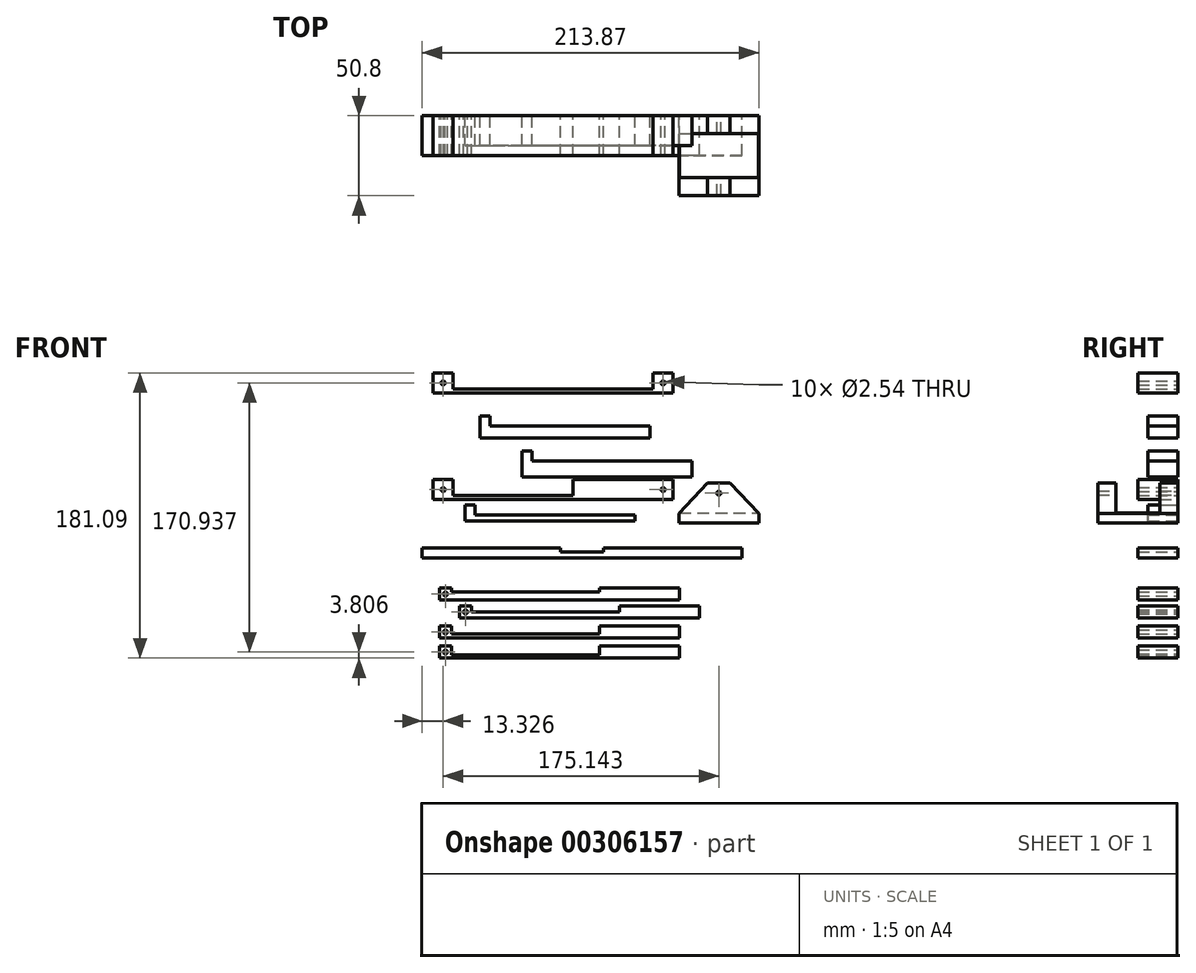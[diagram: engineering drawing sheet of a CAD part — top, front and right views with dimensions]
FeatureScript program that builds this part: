
annotation { "Feature Type Name" : "Feature", "Feature Type Description" : "" }
export const myFeature = defineFeature(function(context is Context, id is Id, definition is map)
    precondition{}
    {
        {
            var Q0;
            Q0=qCreatedBy(makeId("Front.planeOp"),FACE);
            var sketch = newSketch(context, id + "F0", { "sketchPlane" : qUnion([Q0])});
            skLineSegment(sketch, "E0", {"start": v(-69.54, -19.01) * mm, "end": v(133.66, -19.01) * mm});
            skLineSegment(sketch, "E1", {"start": v(133.66, -19.01) * mm, "end": v(133.66, -12.66) * mm});
            skLineSegment(sketch, "E2", {"start": v(133.66, -12.66) * mm, "end": v(45.7, -12.66) * mm});
            skLineSegment(sketch, "E3", {"start": v(45.7, -12.66) * mm, "end": v(45.7, -15.2) * mm});
            skLineSegment(sketch, "E4", {"start": v(45.7, -15.2) * mm, "end": v(18.4, -15.2) * mm});
            skLineSegment(sketch, "E5", {"start": v(18.4, -15.2) * mm, "end": v(18.4, -12.66) * mm});
            skLineSegment(sketch, "E6", {"start": v(18.4, -12.66) * mm, "end": v(-69.54, -12.66) * mm});
            skLineSegment(sketch, "E7", {"start": v(-69.54, -12.66) * mm, "end": v(-69.54, -19.01) * mm});
            skSolve(sketch);
        }
        {
            var Q0;
            Q0 = qSketchRegion(id + "F0", true);
            extrude(context, id + "F1", {"entities" : qUnion([Q0]), "depth" : 25.4 * mm});
        }
        {
            var Q0;
            Q0=qCreatedBy(makeId("Front.planeOp"),FACE);
            var sketch = newSketch(context, id + "F2", { "sketchPlane" : qUnion([Q0])});
            skLineSegment(sketch, "E8", {"start": v(-62.56, 18.1) * mm, "end": v(89.84, 18.1) * mm});
            skLineSegment(sketch, "E9", {"start": v(89.84, 18.1) * mm, "end": v(89.84, 30.8) * mm});
            skLineSegment(sketch, "E10", {"start": v(89.84, 30.8) * mm, "end": v(77.14, 30.8) * mm});
            skLineSegment(sketch, "E11", {"start": v(77.14, 30.8) * mm, "end": v(77.14, 20.64) * mm});
            skLineSegment(sketch, "E12", {"start": v(77.14, 20.64) * mm, "end": v(-49.86, 20.64) * mm});
            skLineSegment(sketch, "E13", {"start": v(-49.86, 20.64) * mm, "end": v(-49.86, 30.8) * mm});
            skLineSegment(sketch, "E14", {"start": v(-49.86, 30.8) * mm, "end": v(-62.56, 30.8) * mm});
            skLineSegment(sketch, "E15", {"start": v(-62.56, 30.8) * mm, "end": v(-62.56, 18.1) * mm});
            skCircle(sketch, "E16", {"center": v(-56.21, 24.45) * mm, "radius": 1.27 * mm});
            skPoint(sketch, "E16.centerSnap0", {"position": v(-56.21, 30.8) * mm});
            skPoint(sketch, "E16.centerSnap1", {"position": v(-62.56, 24.45) * mm});
            skCircle(sketch, "E17", {"center": v(83.49, 24.45) * mm, "radius": 1.27 * mm});
            skPoint(sketch, "E17.centerSnap0", {"position": v(89.84, 24.45) * mm});
            skPoint(sketch, "E17.centerSnap1", {"position": v(83.49, 30.8) * mm});
            skSolve(sketch);
        }
        {
            var Q0;
            Q0 = qSketchRegion(id + "F2", true);
            extrude(context, id + "F3", {"entities" : qUnion([Q0]), "depth" : 25.4 * mm});
        }
        {
            var Q0;
            Q0=qCreatedBy(makeId("Front.planeOp"),FACE);
            var sketch = newSketch(context, id + "F4", { "sketchPlane" : qUnion([Q0])});
            skLineSegment(sketch, "E18", {"start": v(111.75, 28.6) * mm, "end": v(126.1, 28.6) * mm});
            skLineSegment(sketch, "E19", {"start": v(126.1, 28.6) * mm, "end": v(144.33, 9.27) * mm});
            skLineSegment(sketch, "E20", {"start": v(144.33, 9.27) * mm, "end": v(144.33, 3.2) * mm});
            skLineSegment(sketch, "E21", {"start": v(144.33, 3.2) * mm, "end": v(93.53, 3.2) * mm});
            skLineSegment(sketch, "E22", {"start": v(93.53, 3.2) * mm, "end": v(93.53, 9.27) * mm});
            skLineSegment(sketch, "E23", {"start": v(93.53, 9.27) * mm, "end": v(111.75, 28.6) * mm});
            skCircle(sketch, "E24", {"center": v(118.93, 22.25) * mm, "radius": 1.27 * mm});
            skSolve(sketch);
        }
        {
            var Q0;
            Q0 = qSketchRegion(id + "F4", true);
            extrude(context, id + "F5", {"entities" : qUnion([Q0]), "depth" : 50.8 * mm});
        }
        {
            var Q0;
            Q0=makeQuery(id+"F5.opExtrude","SWEPT_FACE",FACE,{"disambiguationData":[OSD([sQuery(id+"F4.wireOp",EDGE,"E18")])]});
            var sketch = newSketch(context, id + "F6", { "sketchPlane" : qUnion([Q0])});
            skLineSegment(sketch, "E25.bottom", {"start": v(93.53, -11.43) * mm, "end": v(144.33, -11.43) * mm});
            skLineSegment(sketch, "E25.top", {"start": v(93.53, -39.37) * mm, "end": v(144.33, -39.37) * mm});
            skLineSegment(sketch, "E25.left", {"start": v(93.53, -11.43) * mm, "end": v(93.53, -39.37) * mm});
            skLineSegment(sketch, "E25.right", {"start": v(144.33, -11.43) * mm, "end": v(144.33, -39.37) * mm});
            skSolve(sketch);
        }
        {
            var Q0;
            Q0 = qSketchRegion(id + "F6", true);
            extrude(context, id + "F7", {"entities" : qUnion([Q0]), "operationType" : NewBodyOperationType.REMOVE, "oppositeDirection" : true, "depth" : 19.05 * mm});
        }
        {
            var Q0;
            Q0=makeQuery(id+"F5.opExtrude","SWEPT_BODY",BODY,{"disambiguationData":[OSD([sQuery(id+"F4.wireOp",EDGE,"E18"),sQuery(id+"F4.wireOp",EDGE,"E19"),sQuery(id+"F4.wireOp",EDGE,"E20"),sQuery(id+"F4.wireOp",EDGE,"E21"),sQuery(id+"F4.wireOp",EDGE,"E22"),sQuery(id+"F4.wireOp",EDGE,"E23"),sQuery(id+"F4.wireOp",EDGE,"E24")])]});
            transform(context, id + "F8", {"entities" : qUnion([Q0]), "transformType" : TransformType.TRANSLATION_3D, "dx" : 60.96 * mm, "dy" : 0 * mm, "dz" : 0 * mm, "makeCopy" : true});
        }
        {
            var Q0;
            Q0=makeQuery(id+"F3.opExtrude","SWEPT_BODY",BODY,{"disambiguationData":[OSD([sQuery(id+"F2.wireOp",EDGE,"E8"),sQuery(id+"F2.wireOp",EDGE,"E9"),sQuery(id+"F2.wireOp",EDGE,"E10"),sQuery(id+"F2.wireOp",EDGE,"E11"),sQuery(id+"F2.wireOp",EDGE,"E12"),sQuery(id+"F2.wireOp",EDGE,"E13"),sQuery(id+"F2.wireOp",EDGE,"E14"),sQuery(id+"F2.wireOp",EDGE,"E15"),sQuery(id+"F2.wireOp",EDGE,"E16"),sQuery(id+"F2.wireOp",EDGE,"E17")])]});
            transform(context, id + "F9", {"entities" : qUnion([Q0]), "transformType" : TransformType.TRANSLATION_3D, "dx" : 0 * mm, "dy" : 0 * mm, "dz" : 67.82 * mm, "makeCopy" : true});
        }
        {
            var Q0;
            Q0=makeQuery(id+"F3.opExtrude","SWEPT_BODY",BODY,{"disambiguationData":[OSD([sQuery(id+"F2.wireOp",EDGE,"E8"),sQuery(id+"F2.wireOp",EDGE,"E9"),sQuery(id+"F2.wireOp",EDGE,"E10"),sQuery(id+"F2.wireOp",EDGE,"E11"),sQuery(id+"F2.wireOp",EDGE,"E12"),sQuery(id+"F2.wireOp",EDGE,"E13"),sQuery(id+"F2.wireOp",EDGE,"E14"),sQuery(id+"F2.wireOp",EDGE,"E15"),sQuery(id+"F2.wireOp",EDGE,"E16"),sQuery(id+"F2.wireOp",EDGE,"E17")])]});
            transform(context, id + "F10", {"entities" : qUnion([Q0]), "transformType" : TransformType.TRANSLATION_3D, "dx" : 0 * mm, "dy" : 0 * mm, "dz" : 33.78 * mm, "makeCopy" : true});
        }
        {
            var Q0;
            Q0=makeQuery(id+"F10.opPattern","COPY",BODY,{"derivedFrom":makeQuery(id+"F3.opExtrude","SWEPT_BODY",BODY,{"disambiguationData":[OSD([sQuery(id+"F2.wireOp",EDGE,"E8"),sQuery(id+"F2.wireOp",EDGE,"E9"),sQuery(id+"F2.wireOp",EDGE,"E10"),sQuery(id+"F2.wireOp",EDGE,"E11"),sQuery(id+"F2.wireOp",EDGE,"E12"),sQuery(id+"F2.wireOp",EDGE,"E13"),sQuery(id+"F2.wireOp",EDGE,"E14"),sQuery(id+"F2.wireOp",EDGE,"E15"),sQuery(id+"F2.wireOp",EDGE,"E16"),sQuery(id+"F2.wireOp",EDGE,"E17")])]}),"instanceName":"1"});
            deleteBodies(context, id + "F11", {"entities" : qUnion([Q0])});
        }
        {
            var Q0;
            Q0=makeQuery(id+"F8.opPattern","COPY",BODY,{"derivedFrom":makeQuery(id+"F5.opExtrude","SWEPT_BODY",BODY,{"disambiguationData":[OSD([sQuery(id+"F4.wireOp",EDGE,"E18"),sQuery(id+"F4.wireOp",EDGE,"E19"),sQuery(id+"F4.wireOp",EDGE,"E20"),sQuery(id+"F4.wireOp",EDGE,"E21"),sQuery(id+"F4.wireOp",EDGE,"E22"),sQuery(id+"F4.wireOp",EDGE,"E23"),sQuery(id+"F4.wireOp",EDGE,"E24")])]}),"instanceName":"1"});
            deleteBodies(context, id + "F12", {"entities" : qUnion([Q0])});
        }
        {
            var Q0;
            Q0=makeQuery(id+"F3.opExtrude","SWEPT_FACE",FACE,{"disambiguationData":[OSD([sQuery(id+"F2.wireOp",EDGE,"E11")])]});
            extrude(context, id + "F13", {"entities" : qUnion([Q0]), "operationType" : NewBodyOperationType.ADD, "depth" : 50.8 * mm});
        }
        {
            var Q0;
            Q0=qCreatedBy(makeId("Front.planeOp"),FACE);
            var sketch = newSketch(context, id + "F14", { "sketchPlane" : qUnion([Q0])});
            skLineSegment(sketch, "E26", {"start": v(-45.79, -49.45) * mm, "end": v(-45.79, -57.07) * mm});
            skLineSegment(sketch, "E27", {"start": v(-45.79, -57.07) * mm, "end": v(106.61, -57.07) * mm});
            skLineSegment(sketch, "E28", {"start": v(106.61, -57.07) * mm, "end": v(106.61, -49.45) * mm});
            skLineSegment(sketch, "E29", {"start": v(106.61, -49.45) * mm, "end": v(55.81, -49.45) * mm});
            skLineSegment(sketch, "E30", {"start": v(55.81, -49.45) * mm, "end": v(55.81, -53.26) * mm});
            skLineSegment(sketch, "E31", {"start": v(55.81, -53.26) * mm, "end": v(-38.17, -53.26) * mm});
            skLineSegment(sketch, "E32", {"start": v(-38.17, -53.26) * mm, "end": v(-38.17, -49.45) * mm});
            skLineSegment(sketch, "E33", {"start": v(-38.17, -49.45) * mm, "end": v(-45.79, -49.45) * mm});
            skCircle(sketch, "E34", {"center": v(-41.98, -53.26) * mm, "radius": 1.27 * mm});
            skSolve(sketch);
        }
        {
            var Q0;
            Q0=qCreatedBy(makeId("Front.planeOp"),FACE);
            var sketch = newSketch(context, id + "F15", { "sketchPlane" : qUnion([Q0])});
            skLineSegment(sketch, "E35", {"start": v(-58.56, -38.02) * mm, "end": v(-58.56, -45.64) * mm});
            skLineSegment(sketch, "E36", {"start": v(-58.56, -45.64) * mm, "end": v(93.84, -45.64) * mm});
            skLineSegment(sketch, "E37", {"start": v(93.84, -45.64) * mm, "end": v(93.84, -38.02) * mm});
            skLineSegment(sketch, "E38", {"start": v(93.84, -38.02) * mm, "end": v(43.04, -38.02) * mm});
            skLineSegment(sketch, "E39", {"start": v(43.04, -38.02) * mm, "end": v(43.04, -40.56) * mm});
            skLineSegment(sketch, "E40", {"start": v(43.04, -40.56) * mm, "end": v(-50.94, -40.56) * mm});
            skLineSegment(sketch, "E41", {"start": v(-50.94, -40.56) * mm, "end": v(-50.94, -38.02) * mm});
            skLineSegment(sketch, "E42", {"start": v(-50.94, -38.02) * mm, "end": v(-58.56, -38.02) * mm});
            skCircle(sketch, "E43", {"center": v(-54.75, -41.83) * mm, "radius": 1.27 * mm});
            skSolve(sketch);
        }
        {
            var Q0;
            Q0=qCreatedBy(makeId("Front.planeOp"),FACE);
            var sketch = newSketch(context, id + "F16", { "sketchPlane" : qUnion([Q0])});
            skLineSegment(sketch, "E44", {"start": v(-58.56, -62.15) * mm, "end": v(-58.56, -69.77) * mm});
            skLineSegment(sketch, "E45", {"start": v(-58.56, -69.77) * mm, "end": v(93.84, -69.77) * mm});
            skLineSegment(sketch, "E46", {"start": v(93.84, -69.77) * mm, "end": v(93.84, -62.15) * mm});
            skLineSegment(sketch, "E47", {"start": v(93.84, -62.15) * mm, "end": v(43.04, -62.15) * mm});
            skLineSegment(sketch, "E48", {"start": v(43.04, -62.15) * mm, "end": v(43.04, -67.23) * mm});
            skLineSegment(sketch, "E49", {"start": v(43.04, -67.23) * mm, "end": v(-50.94, -67.23) * mm});
            skLineSegment(sketch, "E50", {"start": v(-50.94, -67.23) * mm, "end": v(-50.94, -62.15) * mm});
            skLineSegment(sketch, "E51", {"start": v(-50.94, -62.15) * mm, "end": v(-58.56, -62.15) * mm});
            skCircle(sketch, "E52", {"center": v(-54.75, -65.96) * mm, "radius": 1.27 * mm});
            skSolve(sketch);
        }
        {
            var Q0;
            Q0=qCreatedBy(makeId("Front.planeOp"),FACE);
            var sketch = newSketch(context, id + "F17", { "sketchPlane" : qUnion([Q0])});
            skLineSegment(sketch, "E53", {"start": v(-58.56, -74.85) * mm, "end": v(-58.56, -82.47) * mm});
            skLineSegment(sketch, "E54", {"start": v(-58.56, -82.47) * mm, "end": v(93.84, -82.47) * mm});
            skLineSegment(sketch, "E55", {"start": v(93.84, -82.47) * mm, "end": v(93.84, -74.85) * mm});
            skLineSegment(sketch, "E56", {"start": v(93.84, -74.85) * mm, "end": v(43.04, -74.85) * mm});
            skLineSegment(sketch, "E57", {"start": v(43.04, -74.85) * mm, "end": v(43.04, -80.57) * mm});
            skLineSegment(sketch, "E58", {"start": v(43.04, -80.57) * mm, "end": v(-50.94, -80.57) * mm});
            skLineSegment(sketch, "E59", {"start": v(-50.94, -80.57) * mm, "end": v(-50.94, -74.85) * mm});
            skLineSegment(sketch, "E60", {"start": v(-50.94, -74.85) * mm, "end": v(-58.56, -74.85) * mm});
            skCircle(sketch, "E61", {"center": v(-54.75, -78.66) * mm, "radius": 1.27 * mm});
            skSolve(sketch);
        }
        {
            var Q0;
            Q0=makeQuery(id+"F15.imprint","IMPRINT",FACE,{"disambiguationData":[TD([[makeQuery(id+"F15.imprint","IMPRINT",EDGE,{"derivedFrom":sQuery(id+"F15.wireOp",EDGE,"E35")}),1.0]])]});
            var Q1;
            Q1=makeQuery(id+"F14.imprint","IMPRINT",FACE,{"disambiguationData":[TD([[makeQuery(id+"F14.imprint","IMPRINT",EDGE,{"derivedFrom":sQuery(id+"F14.wireOp",EDGE,"E26")}),1.0]])]});
            var Q2;
            Q2=makeQuery(id+"F16.imprint","IMPRINT",FACE,{"disambiguationData":[TD([[makeQuery(id+"F16.imprint","IMPRINT",EDGE,{"derivedFrom":sQuery(id+"F16.wireOp",EDGE,"E44")}),1.0]])]});
            var Q3;
            Q3=makeQuery(id+"F17.imprint","IMPRINT",FACE,{"disambiguationData":[TD([[makeQuery(id+"F17.imprint","IMPRINT",EDGE,{"derivedFrom":sQuery(id+"F17.wireOp",EDGE,"E53")}),1.0]])]});
            extrude(context, id + "F18", {"entities" : qUnion([Q0, Q1, Q2, Q3]), "depth" : 25.4 * mm});
        }
        {
            var Q0;
            Q0=qCreatedBy(makeId("Front.planeOp"),FACE);
            var sketch = newSketch(context, id + "F19", { "sketchPlane" : qUnion([Q0])});
            skLineSegment(sketch, "E62", {"start": v(-32.9, 57.4) * mm, "end": v(-32.9, 71.36) * mm});
            skLineSegment(sketch, "E63", {"start": v(-32.9, 71.36) * mm, "end": v(-26.55, 71.36) * mm});
            skLineSegment(sketch, "E64", {"start": v(-26.55, 71.36) * mm, "end": v(-26.55, 65.01) * mm});
            skLineSegment(sketch, "E65", {"start": v(-26.55, 65.01) * mm, "end": v(75.05, 65.01) * mm});
            skLineSegment(sketch, "E66", {"start": v(75.05, 65.01) * mm, "end": v(75.05, 57.4) * mm});
            skLineSegment(sketch, "E67", {"start": v(75.05, 57.4) * mm, "end": v(-32.9, 57.4) * mm});
            skSolve(sketch);
        }
        {
            var Q0;
            Q0 = qSketchRegion(id + "F19", true);
            extrude(context, id + "F20", {"entities" : qUnion([Q0]), "depth" : 19.05 * mm});
        }
        {
            var Q0;
            Q0=qCreatedBy(makeId("Front.planeOp"),FACE);
            var sketch = newSketch(context, id + "F21", { "sketchPlane" : qUnion([Q0])});
            skLineSegment(sketch, "E68", {"start": v(0.34, 42.61) * mm, "end": v(101.94, 42.61) * mm});
            skLineSegment(sketch, "E69", {"start": v(101.94, 42.61) * mm, "end": v(101.94, 32.45) * mm});
            skLineSegment(sketch, "E70", {"start": v(101.94, 32.45) * mm, "end": v(-6, 32.45) * mm});
            skLineSegment(sketch, "E71", {"start": v(-6, 32.45) * mm, "end": v(-6, 48.96) * mm});
            skLineSegment(sketch, "E72", {"start": v(-6, 48.96) * mm, "end": v(0.34, 48.96) * mm});
            skLineSegment(sketch, "E73", {"start": v(0.34, 48.96) * mm, "end": v(0.34, 42.61) * mm});
            skSolve(sketch);
        }
        {
            var Q0;
            Q0 = qSketchRegion(id + "F21", true);
            extrude(context, id + "F22", {"entities" : qUnion([Q0]), "depth" : 19.05 * mm});
        }
        {
            var Q0;
            Q0=qCreatedBy(makeId("Front.planeOp"),FACE);
            var sketch = newSketch(context, id + "F23", { "sketchPlane" : qUnion([Q0])});
            skLineSegment(sketch, "E74", {"start": v(-35.85, 8.52) * mm, "end": v(65.75, 8.52) * mm});
            skLineSegment(sketch, "E75", {"start": v(65.75, 8.52) * mm, "end": v(65.75, 4.71) * mm});
            skLineSegment(sketch, "E76", {"start": v(65.75, 4.71) * mm, "end": v(-42.2, 4.71) * mm});
            skLineSegment(sketch, "E77", {"start": v(-42.2, 4.71) * mm, "end": v(-42.2, 14.87) * mm});
            skLineSegment(sketch, "E78", {"start": v(-42.2, 14.87) * mm, "end": v(-35.85, 14.87) * mm});
            skLineSegment(sketch, "E79", {"start": v(-35.85, 14.87) * mm, "end": v(-35.85, 8.52) * mm});
            skSolve(sketch);
        }
        {
            var Q0;
            Q0 = qSketchRegion(id + "F23", true);
            extrude(context, id + "F24", {"entities" : qUnion([Q0]), "depth" : 19.05 * mm});
        }
    });
